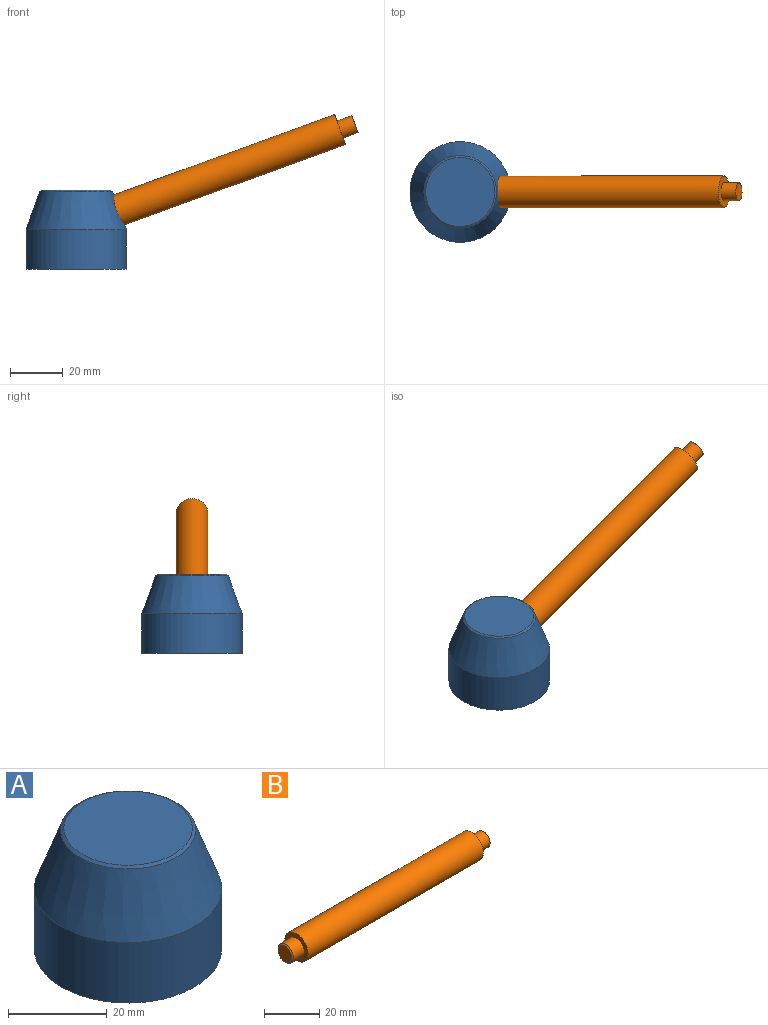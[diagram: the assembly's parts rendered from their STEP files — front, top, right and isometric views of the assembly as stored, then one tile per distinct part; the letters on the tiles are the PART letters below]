
ASSEMBLY  parts=2 mates=1
PART A: 11 faces, bbox 38x38x30 mm
  f0: cone r=19mm half-angle=20deg, axis (0,0,-1), area 1474.1mm2, adj f2,f4,f5
  f1: plane 26.08x26.08mm, normal (0,0,1), area 534.2mm2, adj f4
  f2: cylinder r=19mm len=38mm, axis (0,0,1), area 1790.7mm2, adj f0,f3
  f3: plane 38x38mm, normal (0,0,-1), area 865.3mm2, adj f2,f9
  f4: cone r=13.04mm half-angle=55deg, axis (0,0,-1), area 68.8mm2, adj f0,f1
  f5: cylinder r=6mm len=12mm, axis (0.94,0,0.34), area 27mm2, adj f0,f6
  f6: plane 12x11.28mm, normal (0.94,0,0.34), area 76.8mm2, adj f5,f7
  f7: cylinder r=3.4mm len=10.55mm, axis (0.94,0,0.34), area 186.9mm2, adj f6,f8
  f8: cone r=0mm half-angle=59deg, axis (0.94,0,0.34), area 42.4mm2, adj f7
  f9: cylinder r=9.25mm len=18.5mm, axis (0,0,-1), area 871.8mm2, adj f3,f10
  f10: cone r=0mm half-angle=59deg, axis (0,0,-1), area 313.6mm2, adj f9
PART B: 8 faces, bbox 102x12x12 mm
  f0: cylinder r=4mm len=8mm, axis (1,0,0), area 138.2mm2, adj f4,f5
  f1: plane 7x7mm, normal (-1,0,0), area 38.5mm2, adj f5
  f2: cylinder r=6mm len=90mm, axis (-1,0,0), area 3392.9mm2, adj f3,f4
  f3: plane 12x12mm, normal (1,0,0), area 76.8mm2, adj f2,f6
  f4: plane 12x12mm, normal (-1,0,0), area 62.8mm2, adj f0,f2
  f5: cone r=4mm half-angle=45deg, axis (1,0,0), area 16.7mm2, adj f0,f1
  f6: cylinder r=3.4mm len=6.8mm, axis (-1,0,0), area 128.2mm2, adj f3,f7
  f7: plane 6.8x6.8mm, normal (1,0,0), area 36.3mm2, adj f6
PLACE A at identity fixed
PLACE B rot(axis=(0,-1,0),20deg) t=(15.1,-42.58,7.07)mm
MATE fastened B.f0 <-> A.f5  axis (-0.94,0,-0.34) through (15.1,0,7.07)mm
